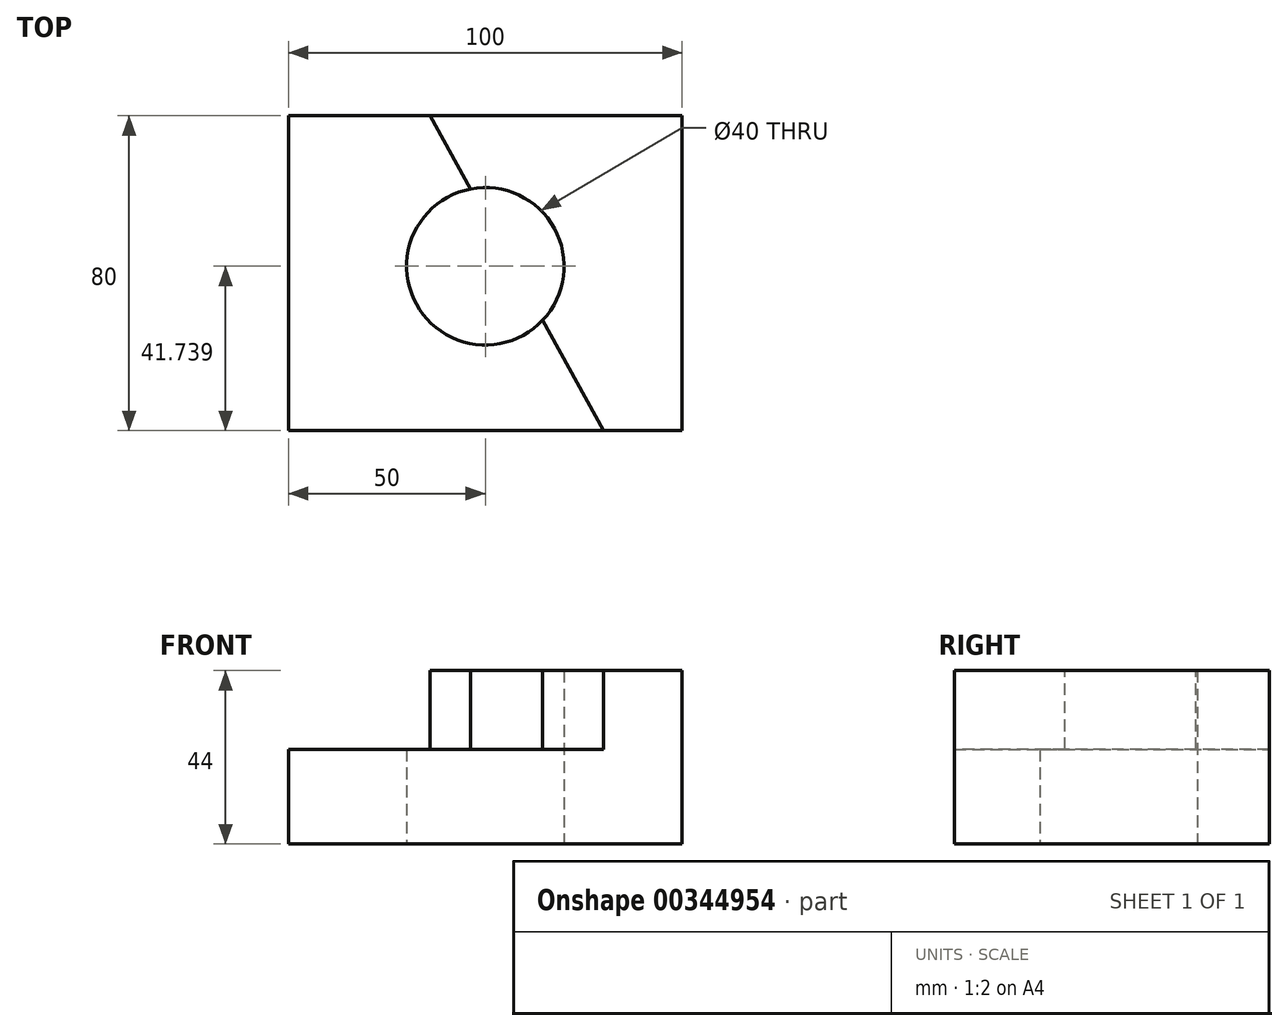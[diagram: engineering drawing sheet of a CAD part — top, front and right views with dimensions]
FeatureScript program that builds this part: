
annotation { "Feature Type Name" : "Feature", "Feature Type Description" : "" }
export const myFeature = defineFeature(function(context is Context, id is Id, definition is map)
    precondition{}
    {
        {
            var Q0;
            Q0=qCreatedBy(makeId("Top.planeOp"),FACE);
            var sketch = newSketch(context, id + "F0", { "sketchPlane" : qUnion([Q0])});
            skLineSegment(sketch, "E0.bottom", {"start": v(-50, -40) * mm, "end": v(50, -40) * mm});
            skLineSegment(sketch, "E0.top", {"start": v(-50, 40) * mm, "end": v(50, 40) * mm});
            skLineSegment(sketch, "E0.left", {"start": v(-50, -40) * mm, "end": v(-50, 40) * mm});
            skLineSegment(sketch, "E0.right", {"start": v(50, -40) * mm, "end": v(50, 40) * mm});
            skPoint(sketch, "E0.middle", {"position": v(0, 0) * mm});
            skCircle(sketch, "E1", {"center": v(0, 1.74) * mm, "radius": 20 * mm});
            skSolve(sketch);
        }
        {
            var Q0;
            Q0 = qSketchRegion(id + "F0", true);
            extrude(context, id + "F1", {"entities" : qUnion([Q0]), "depth" : 44 * mm});
        }
        {
            var Q0;
            Q0 = qSketchRegion(id + "F0", true);
            extrude(context, id + "F2", {"entities" : qUnion([Q0]), "operationType" : NewBodyOperationType.ADD, "depth" : 44 * mm});
        }
        {
            var Q0;
            Q0=makeQuery(id+"F1.opExtrude","CAP_FACE",FACE,{"disambiguationData":[OSD([sQuery(id+"F0.wireOp",EDGE,"E0.bottom"),sQuery(id+"F0.wireOp",EDGE,"E0.top"),sQuery(id+"F0.wireOp",EDGE,"E0.left"),sQuery(id+"F0.wireOp",EDGE,"E0.right"),sQuery(id+"F0.wireOp",EDGE,"E1")])],"isStart":false});
            var sketch = newSketch(context, id + "F3", { "sketchPlane" : qUnion([Q0])});
            skPoint(sketch, "E2", {"position": v(-14, 40) * mm});
            skPoint(sketch, "E3", {"position": v(30, -40) * mm});
            skPoint(sketch, "E4", {"position": v(-50, 40) * mm});
            skPoint(sketch, "E5", {"position": v(-50, -40) * mm});
            skLineSegment(sketch, "E6", {"start": v(-14, 40) * mm, "end": v(30, -40) * mm});
            skSolve(sketch);
        }
        {
            var Q0;
            {var subQ0=makeQuery(id+"F1.opExtrude","CAP_EDGE",EDGE,{"disambiguationData":[OSD([sQuery(id+"F0.wireOp",EDGE,"E0.left")])],"isStart":false});Q0=makeQuery(id+"F3.imprint","IMPRINT",FACE,{"disambiguationData":[TD([[makeQuery(id+"F3.imprint","IMPRINT",EDGE,{"derivedFrom":subQ0}),-1.0]])]});}
            extrude(context, id + "F4", {"entities" : qUnion([Q0]), "operationType" : NewBodyOperationType.REMOVE, "oppositeDirection" : true, "depth" : 20 * mm});
        }
    });
